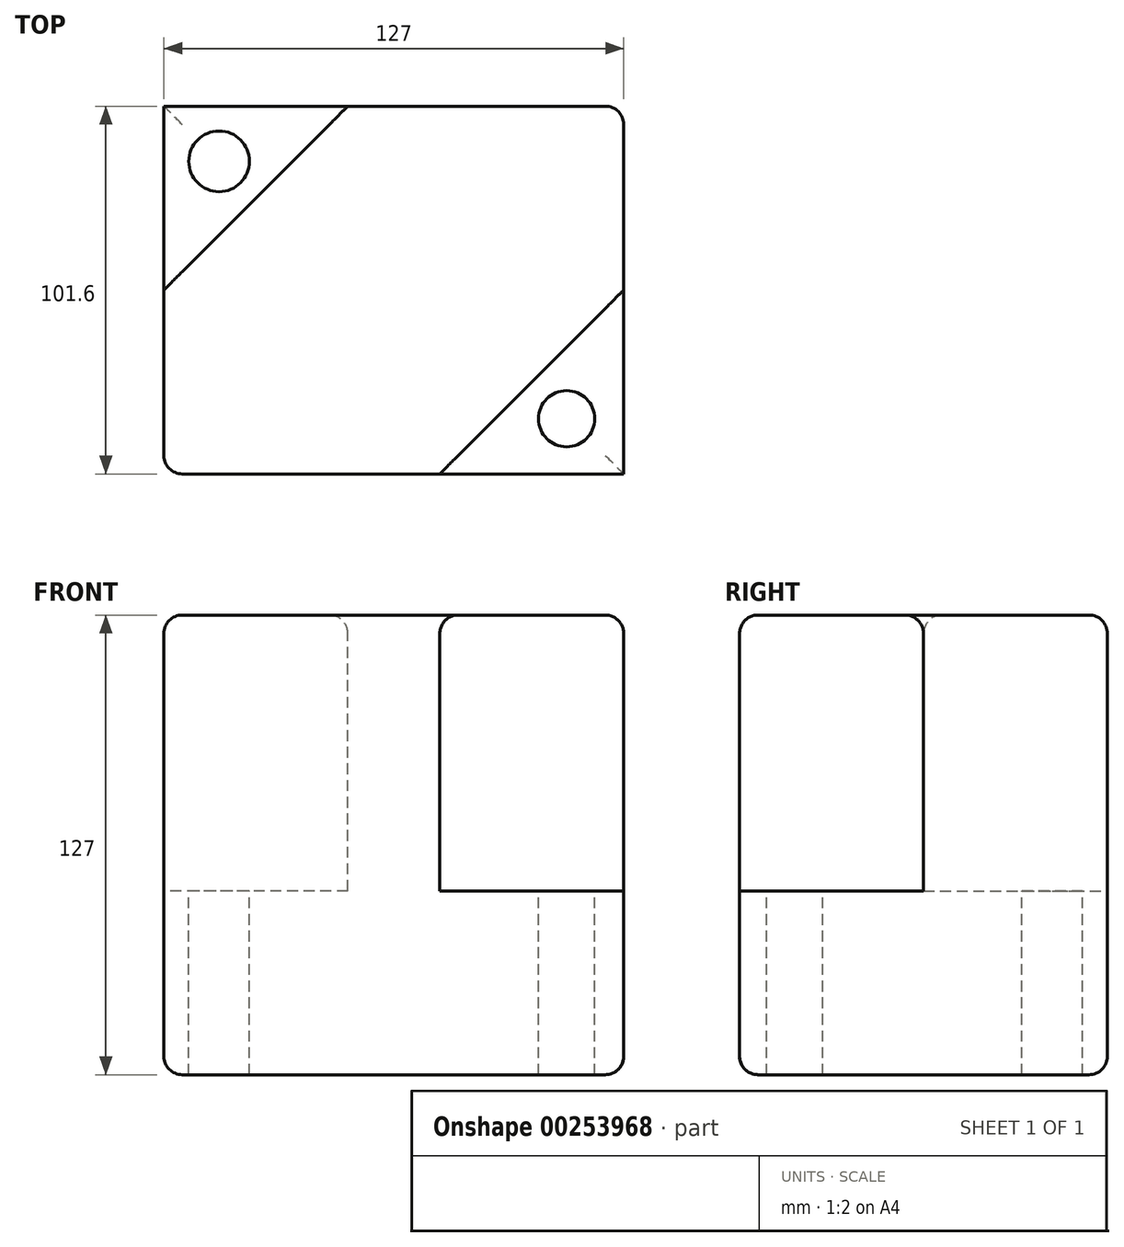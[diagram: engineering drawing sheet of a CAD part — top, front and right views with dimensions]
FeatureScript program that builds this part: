
annotation { "Feature Type Name" : "Feature", "Feature Type Description" : "" }
export const myFeature = defineFeature(function(context is Context, id is Id, definition is map)
    precondition{}
    {
        {
            var Q0;
            Q0=qCreatedBy(makeId("Front.planeOp"),FACE);
            var sketch = newSketch(context, id + "F0", { "sketchPlane" : qUnion([Q0])});
            skLineSegment(sketch, "E0.bottom", {"start": v(63.5, -63.5) * mm, "end": v(-63.5, -63.5) * mm});
            skLineSegment(sketch, "E0.top", {"start": v(63.5, 63.5) * mm, "end": v(-63.5, 63.5) * mm});
            skLineSegment(sketch, "E0.left", {"start": v(63.5, -63.5) * mm, "end": v(63.5, 63.5) * mm});
            skLineSegment(sketch, "E0.right", {"start": v(-63.5, -63.5) * mm, "end": v(-63.5, 63.5) * mm});
            skPoint(sketch, "E0.middle", {"position": v(0, 0) * mm});
            skSolve(sketch);
        }
        {
            var Q0;
            Q0=makeQuery(id+"F0.imprint","IMPRINT",FACE,{"disambiguationData":[TD([[makeQuery(id+"F0.imprint","IMPRINT",EDGE,{"derivedFrom":sQuery(id+"F0.wireOp",EDGE,"E0.bottom")}),-1.0]])]});
            extrude(context, id + "F1", {"entities" : qUnion([Q0]), "depth" : 101.6 * mm});
        }
        {
            var Q0;
            Q0=makeQuery(id+"F1.opExtrude","SWEPT_FACE",FACE,{"disambiguationData":[OSD([sQuery(id+"F0.wireOp",EDGE,"E0.top")])]});
            var sketch = newSketch(context, id + "F2", { "sketchPlane" : qUnion([Q0])});
            skLineSegment(sketch, "E1", {"start": v(-63.5, 0) * mm, "end": v(-63.5, -50.8) * mm});
            skLineSegment(sketch, "E2", {"start": v(-63.5, -50.8) * mm, "end": v(-12.7, 0) * mm});
            skLineSegment(sketch, "E3", {"start": v(-12.7, 0) * mm, "end": v(-63.5, 0) * mm});
            skLineSegment(sketch, "E4", {"start": v(63.5, -101.6) * mm, "end": v(63.5, -50.8) * mm});
            skLineSegment(sketch, "E5", {"start": v(63.5, -50.8) * mm, "end": v(12.7, -101.6) * mm});
            skLineSegment(sketch, "E6", {"start": v(12.7, -101.6) * mm, "end": v(63.5, -101.6) * mm});
            skSolve(sketch);
        }
        {
            var Q0;
            Q0=makeQuery(id+"F2.imprint","IMPRINT",FACE,{"disambiguationData":[TD([[makeQuery(id+"F2.imprint","IMPRINT",EDGE,{"derivedFrom":sQuery(id+"F2.wireOp",EDGE,"E1")}),-1.0]])]});
            var Q1;
            Q1=sQuery(id+"F2.wireOp",EDGE,"E1");
            var Q2;
            Q2=sQuery(id+"F2.wireOp",EDGE,"E2");
            var Q3;
            Q3=sQuery(id+"F2.wireOp",EDGE,"E3");
            extrude(context, id + "F3", {"entities" : qUnion([Q0]), "operationType" : NewBodyOperationType.REMOVE, "surfaceEntities" : qUnion([Q1, Q2, Q3]), "oppositeDirection" : true, "depth" : 76.2 * mm});
        }
        {
            var Q0;
            Q0=makeQuery(id+"F1.opExtrude","SWEPT_FACE",FACE,{"disambiguationData":[OSD([sQuery(id+"F0.wireOp",EDGE,"E0.top")])]});
            var sketch = newSketch(context, id + "F4", { "sketchPlane" : qUnion([Q0])});
            skLineSegment(sketch, "E7", {"start": v(63.5, -101.6) * mm, "end": v(63.5, -50.8) * mm});
            skLineSegment(sketch, "E8", {"start": v(63.5, -50.8) * mm, "end": v(12.7, -101.6) * mm});
            skLineSegment(sketch, "E9", {"start": v(12.7, -101.6) * mm, "end": v(63.5, -101.6) * mm});
            skSolve(sketch);
        }
        {
            var Q0;
            Q0=makeQuery(id+"F4.imprint","IMPRINT",FACE,{"disambiguationData":[TD([[makeQuery(id+"F4.imprint","IMPRINT",EDGE,{"derivedFrom":sQuery(id+"F4.wireOp",EDGE,"E7")}),1.0]])]});
            extrude(context, id + "F5", {"entities" : qUnion([Q0]), "operationType" : NewBodyOperationType.REMOVE, "oppositeDirection" : true, "depth" : 76.2 * mm});
        }
        {
            var Q0;
            Q0=makeQuery(id+"F5.boolean.opBoolean","COPY",FACE,{"derivedFrom":makeQuery(id+"F5.opExtrude","CAP_FACE",FACE,{"disambiguationData":[OSD([sQuery(id+"F4.wireOp",EDGE,"E7"),sQuery(id+"F4.wireOp",EDGE,"E8"),sQuery(id+"F4.wireOp",EDGE,"E9")])],"isStart":false})});
            var sketch = newSketch(context, id + "F6", { "sketchPlane" : qUnion([Q0])});
            skCircle(sketch, "E10", {"center": v(47.73, -86.36) * mm, "radius": 7.77 * mm});
            skSolve(sketch);
        }
        {
            var Q0;
            Q0=makeQuery(id+"F3.boolean.opBoolean","COPY",FACE,{"derivedFrom":makeQuery(id+"F3.opExtrude","CAP_FACE",FACE,{"disambiguationData":[OSD([sQuery(id+"F2.wireOp",EDGE,"E1"),sQuery(id+"F2.wireOp",EDGE,"E2"),sQuery(id+"F2.wireOp",EDGE,"E3")])],"isStart":false})});
            var sketch = newSketch(context, id + "F7", { "sketchPlane" : qUnion([Q0])});
            skCircle(sketch, "E11", {"center": v(-48.26, -15.24) * mm, "radius": 8.38 * mm});
            skSolve(sketch);
        }
        {
            var Q0;
            Q0=makeQuery(id+"F7.imprint","IMPRINT",FACE,{"disambiguationData":[TD([[makeQuery(id+"F7.imprint","IMPRINT",EDGE,{"derivedFrom":sQuery(id+"F7.wireOp",EDGE,"E11")}),1.0]])]});
            var Q1;
            Q1=sQuery(id+"F7.wireOp",EDGE,"E11");
            extrude(context, id + "F8", {"entities" : qUnion([Q0]), "operationType" : NewBodyOperationType.REMOVE, "surfaceEntities" : qUnion([Q1]), "oppositeDirection" : true, "depth" : 50.8 * mm});
        }
        {
            var Q0;
            Q0=makeQuery(id+"F6.imprint","IMPRINT",FACE,{"disambiguationData":[TD([[makeQuery(id+"F6.imprint","IMPRINT",EDGE,{"derivedFrom":sQuery(id+"F6.wireOp",EDGE,"E10")}),1.0]])]});
            extrude(context, id + "F9", {"entities" : qUnion([Q0]), "operationType" : NewBodyOperationType.REMOVE, "oppositeDirection" : true, "depth" : 50.8 * mm});
        }
        {
            var Q0;
            Q0=makeQuery(id+"F3.boolean.opBoolean","COPY",EDGE,{"derivedFrom":makeQuery(id+"F3.opExtrude","CAP_EDGE",EDGE,{"disambiguationData":[OSD([sQuery(id+"F2.wireOp",EDGE,"E2")])],"isStart":true})});
            var Q1;
            Q1=makeQuery(id+"F1.opExtrude","SWEPT_EDGE",EDGE,{"disambiguationData":[OSD([sQuery(id+"F0.wireOp",EDGE,"E0.top"),sQuery(id+"F0.wireOp",EDGE,"E0.right")])]});
            var Q2;
            Q2=makeQuery(id+"F1.opExtrude","CAP_EDGE",EDGE,{"disambiguationData":[OSD([sQuery(id+"F0.wireOp",EDGE,"E0.top")])],"isStart":false});
            var Q3;
            Q3=makeQuery(id+"F5.boolean.opBoolean","COPY",EDGE,{"derivedFrom":makeQuery(id+"F5.opExtrude","CAP_EDGE",EDGE,{"disambiguationData":[OSD([sQuery(id+"F4.wireOp",EDGE,"E8")])],"isStart":true})});
            var Q4;
            Q4=makeQuery(id+"F1.opExtrude","CAP_EDGE",EDGE,{"disambiguationData":[OSD([sQuery(id+"F0.wireOp",EDGE,"E0.top")])],"isStart":true});
            var Q5;
            Q5=makeQuery(id+"F1.opExtrude","SWEPT_EDGE",EDGE,{"disambiguationData":[OSD([sQuery(id+"F0.wireOp",EDGE,"E0.top"),sQuery(id+"F0.wireOp",EDGE,"E0.left")])]});
            var Q6;
            Q6=makeQuery(id+"F5.boolean.opBoolean","COPY",EDGE,{"derivedFrom":makeQuery(id+"F5.opExtrude","SWEPT_EDGE",EDGE,{"disambiguationData":[OSD([sQuery(id+"F0.wireOp",EDGE,"E0.top"),sQuery(id+"F0.wireOp",EDGE,"E0.left"),sQuery(id+"F4.wireOp",EDGE,"E7"),sQuery(id+"F4.wireOp",EDGE,"E8")])]})});
            var Q7;
            Q7=makeQuery(id+"F1.opExtrude","CAP_EDGE",EDGE,{"disambiguationData":[OSD([sQuery(id+"F0.wireOp",EDGE,"E0.left")])],"isStart":true});
            var Q8;
            Q8=makeQuery(id+"F1.opExtrude","SWEPT_EDGE",EDGE,{"disambiguationData":[OSD([sQuery(id+"F0.wireOp",EDGE,"E0.bottom"),sQuery(id+"F0.wireOp",EDGE,"E0.left")])]});
            var Q9;
            Q9=makeQuery(id+"F5.boolean.opBoolean","COPY",EDGE,{"derivedFrom":makeQuery(id+"F5.opExtrude","CAP_EDGE",EDGE,{"disambiguationData":[OSD([sQuery(id+"F4.wireOp",EDGE,"E7")])],"isStart":false})});
            var Q10;
            Q10=makeQuery(id+"F5.boolean.opBoolean","COPY",EDGE,{"derivedFrom":makeQuery(id+"F5.opExtrude","CAP_EDGE",EDGE,{"disambiguationData":[OSD([sQuery(id+"F4.wireOp",EDGE,"E9")])],"isStart":false})});
            var Q11;
            Q11=makeQuery(id+"F5.boolean.opBoolean","COPY",EDGE,{"derivedFrom":makeQuery(id+"F5.opExtrude","SWEPT_EDGE",EDGE,{"disambiguationData":[OSD([sQuery(id+"F0.wireOp",EDGE,"E0.top"),sQuery(id+"F4.wireOp",EDGE,"E8"),sQuery(id+"F4.wireOp",EDGE,"E9")])]})});
            var Q12;
            Q12=makeQuery(id+"F1.opExtrude","CAP_EDGE",EDGE,{"disambiguationData":[OSD([sQuery(id+"F0.wireOp",EDGE,"E0.right")])],"isStart":false});
            var Q13;
            Q13=makeQuery(id+"F1.opExtrude","CAP_EDGE",EDGE,{"disambiguationData":[OSD([sQuery(id+"F0.wireOp",EDGE,"E0.bottom")])],"isStart":false});
            var Q14;
            Q14=makeQuery(id+"F1.opExtrude","SWEPT_EDGE",EDGE,{"disambiguationData":[OSD([sQuery(id+"F0.wireOp",EDGE,"E0.bottom"),sQuery(id+"F0.wireOp",EDGE,"E0.right")])]});
            var Q15;
            Q15=makeQuery(id+"F3.boolean.opBoolean","COPY",EDGE,{"derivedFrom":makeQuery(id+"F3.opExtrude","SWEPT_EDGE",EDGE,{"disambiguationData":[OSD([sQuery(id+"F0.wireOp",EDGE,"E0.top"),sQuery(id+"F0.wireOp",EDGE,"E0.right"),sQuery(id+"F2.wireOp",EDGE,"E1"),sQuery(id+"F2.wireOp",EDGE,"E2")])]})});
            var Q16;
            Q16=makeQuery(id+"F3.boolean.opBoolean","COPY",EDGE,{"derivedFrom":makeQuery(id+"F3.opExtrude","CAP_EDGE",EDGE,{"disambiguationData":[OSD([sQuery(id+"F2.wireOp",EDGE,"E1")])],"isStart":false})});
            var Q17;
            Q17=makeQuery(id+"F1.opExtrude","CAP_EDGE",EDGE,{"disambiguationData":[OSD([sQuery(id+"F0.wireOp",EDGE,"E0.bottom")])],"isStart":true});
            var Q18;
            Q18=makeQuery(id+"F3.boolean.opBoolean","COPY",EDGE,{"derivedFrom":makeQuery(id+"F3.opExtrude","CAP_EDGE",EDGE,{"disambiguationData":[OSD([sQuery(id+"F2.wireOp",EDGE,"E3")])],"isStart":false})});
            var Q19;
            Q19=makeQuery(id+"F3.boolean.opBoolean","COPY",EDGE,{"derivedFrom":makeQuery(id+"F3.opExtrude","SWEPT_EDGE",EDGE,{"disambiguationData":[OSD([sQuery(id+"F0.wireOp",EDGE,"E0.top"),sQuery(id+"F2.wireOp",EDGE,"E2"),sQuery(id+"F2.wireOp",EDGE,"E3")])]})});
            fillet(context, id + "F10", {"entities" : qUnion([Q0, Q1, Q2, Q3, Q4, Q5, Q6, Q7, Q8, Q9, Q10, Q11, Q12, Q13, Q14, Q15, Q16, Q17, Q18, Q19]), "radius" : 5.08 * mm, "tangentPropagation" : true, "allowEdgeOverflow" : false});
        }
    });
